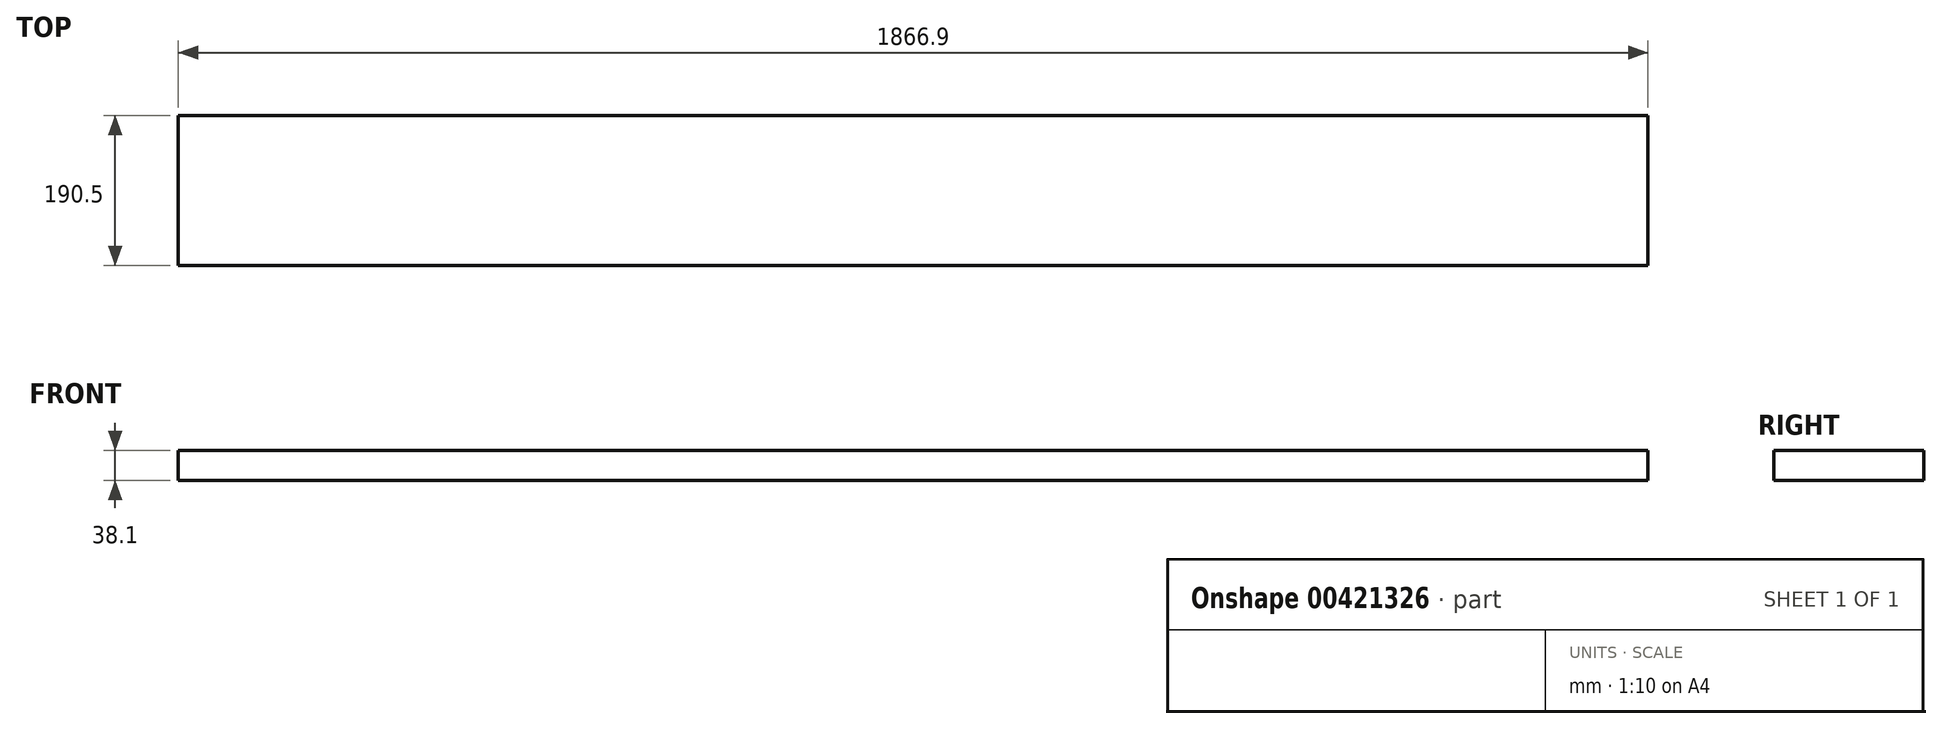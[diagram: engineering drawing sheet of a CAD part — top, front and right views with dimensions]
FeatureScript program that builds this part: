
annotation { "Feature Type Name" : "Feature", "Feature Type Description" : "" }
export const myFeature = defineFeature(function(context is Context, id is Id, definition is map)
    precondition{}
    {
        {
            var Q0;
            Q0=qCreatedBy(makeId("Top.planeOp"),FACE);
            var sketch = newSketch(context, id + "F0", { "sketchPlane" : qUnion([Q0])});
            skLineSegment(sketch, "E0.bottom", {"start": v(-188.15, -82.97) * mm, "end": v(1678.75, -82.97) * mm});
            skLineSegment(sketch, "E0.top", {"start": v(-188.15, 107.53) * mm, "end": v(1678.75, 107.53) * mm});
            skLineSegment(sketch, "E0.left", {"start": v(-188.15, -82.97) * mm, "end": v(-188.15, 107.53) * mm});
            skLineSegment(sketch, "E0.right", {"start": v(1678.75, -82.97) * mm, "end": v(1678.75, 107.53) * mm});
            skSolve(sketch);
        }
        {
            var Q0;
            Q0=makeQuery(id+"F0.imprint","IMPRINT",FACE,{"disambiguationData":[TD([[makeQuery(id+"F0.imprint","IMPRINT",EDGE,{"derivedFrom":sQuery(id+"F0.wireOp",EDGE,"E0.bottom")}),1.0]])]});
            extrude(context, id + "F1", {"entities" : qUnion([Q0]), "depth" : 38.1 * mm});
        }
    });
